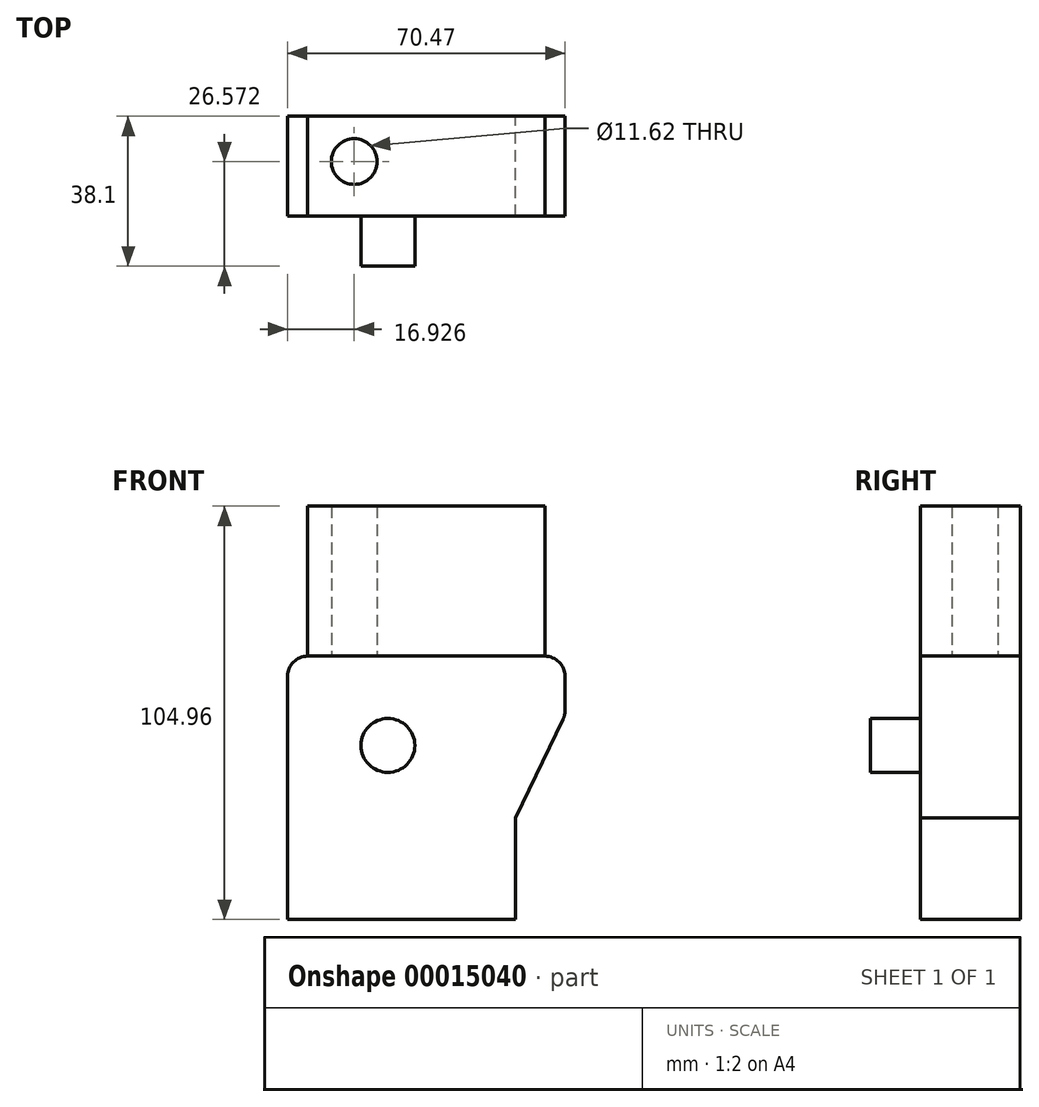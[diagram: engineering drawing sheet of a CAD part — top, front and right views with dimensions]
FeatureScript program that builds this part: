
annotation { "Feature Type Name" : "Feature", "Feature Type Description" : "" }
export const myFeature = defineFeature(function(context is Context, id is Id, definition is map)
    precondition{}
    {
        {
            var Q0;
            Q0=qCreatedBy(makeId("Front.planeOp"),FACE);
            var sketch = newSketch(context, id + "F0", { "sketchPlane" : qUnion([Q0])});
            skLineSegment(sketch, "E0", {"start": v(0, 0) * mm, "end": v(57.96, 0) * mm});
            skLineSegment(sketch, "E1", {"start": v(57.96, 0) * mm, "end": v(57.96, 25.8) * mm});
            skLineSegment(sketch, "E2", {"start": v(57.96, 25.8) * mm, "end": v(70.47, 51.8) * mm});
            skLineSegment(sketch, "E3", {"start": v(70.47, 51.8) * mm, "end": v(70.47, 66.86) * mm});
            skLineSegment(sketch, "E4", {"start": v(70.47, 66.86) * mm, "end": v(0, 66.86) * mm});
            skLineSegment(sketch, "E5", {"start": v(0, 66.86) * mm, "end": v(0, 0) * mm});
            skSolve(sketch);
        }
        {
            var Q0;
            Q0 = qSketchRegion(id + "F0", true);
            extrude(context, id + "F1", {"entities" : qUnion([Q0]), "depth" : 25.4 * mm});
        }
        {
            var Q0;
            Q0=makeQuery(id+"F1.opExtrude","CAP_FACE",FACE,{"disambiguationData":[OSD([sQuery(id+"F0.wireOp",EDGE,"E0"),sQuery(id+"F0.wireOp",EDGE,"E1"),sQuery(id+"F0.wireOp",EDGE,"E2"),sQuery(id+"F0.wireOp",EDGE,"E3"),sQuery(id+"F0.wireOp",EDGE,"E4"),sQuery(id+"F0.wireOp",EDGE,"E5")])],"isStart":false});
            var sketch = newSketch(context, id + "F2", { "sketchPlane" : qUnion([Q0])});
            skCircle(sketch, "E6", {"center": v(25.5, 44.18) * mm, "radius": 6.84 * mm});
            skSolve(sketch);
        }
        {
            var Q0;
            Q0 = qSketchRegion(id + "F2", true);
            extrude(context, id + "F3", {"entities" : qUnion([Q0]), "operationType" : NewBodyOperationType.ADD, "depth" : 12.7 * mm});
        }
        {
            var Q0;
            Q0=makeQuery(id+"F1.opExtrude","SWEPT_EDGE",EDGE,{"disambiguationData":[OSD([sQuery(id+"F0.wireOp",EDGE,"E4"),sQuery(id+"F0.wireOp",EDGE,"E5")])]});
            var Q1;
            Q1=makeQuery(id+"F1.opExtrude","SWEPT_EDGE",EDGE,{"disambiguationData":[OSD([sQuery(id+"F0.wireOp",EDGE,"E3"),sQuery(id+"F0.wireOp",EDGE,"E4")])]});
            var Q2;
            Q2=makeQuery(id+"F1.opExtrude","SWEPT_EDGE",EDGE,{"disambiguationData":[OSD([sQuery(id+"F0.wireOp",EDGE,"E2"),sQuery(id+"F0.wireOp",EDGE,"E3")])]});
            fillet(context, id + "F4", {"entities" : qUnion([Q0, Q1, Q2]), "radius" : 5.08 * mm, "tangentPropagation" : true, "allowEdgeOverflow" : false});
        }
        {
            var Q0;
            Q0=makeQuery(id+"F1.opExtrude","SWEPT_FACE",FACE,{"disambiguationData":[OSD([sQuery(id+"F0.wireOp",EDGE,"E4")])]});
            var sketch = newSketch(context, id + "F5", { "sketchPlane" : qUnion([Q0])});
            skCircle(sketch, "E7", {"center": v(16.93, -11.53) * mm, "radius": 5.81 * mm});
            skSolve(sketch);
        }
        {
            var Q0;
            Q0=makeQuery(id+"F5.imprint","IMPRINT",FACE,{"disambiguationData":[TD([[makeQuery(id+"F5.imprint","IMPRINT",EDGE,{"derivedFrom":sQuery(id+"F5.wireOp",EDGE,"E7")}),-1.0]])]});
            extrude(context, id + "F6", {"entities" : qUnion([Q0]), "depth" : 38.1 * mm});
        }
    });
